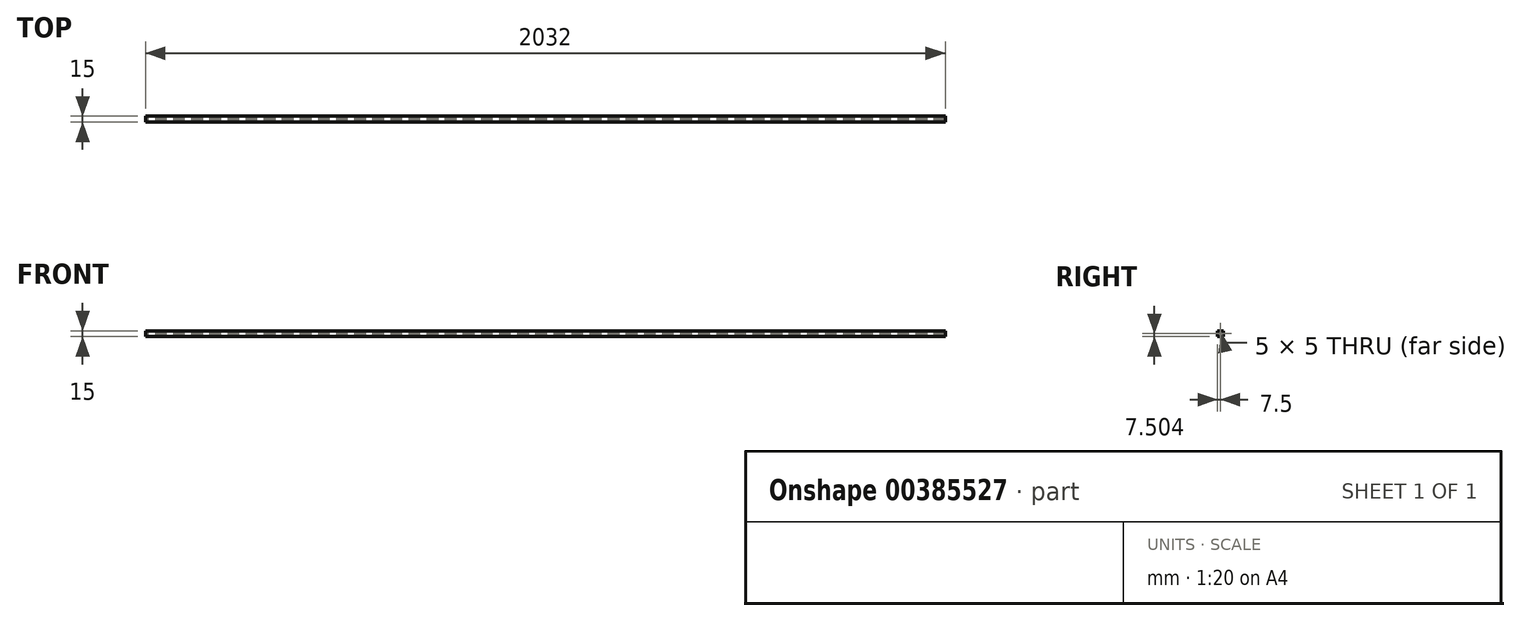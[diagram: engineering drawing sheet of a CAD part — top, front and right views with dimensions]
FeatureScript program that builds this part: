
annotation { "Feature Type Name" : "Feature", "Feature Type Description" : "" }
export const myFeature = defineFeature(function(context is Context, id is Id, definition is map)
    precondition{}
    {
        {
            var Q0;
            Q0=qCreatedBy(makeId("Front.planeOp"),FACE);
            var sketch = newSketch(context, id + "F0", { "sketchPlane" : qUnion([Q0])});
            skLineSegment(sketch, "E0.bottom", {"start": v(-49.25, 39.6) * mm, "end": v(1982.75, 39.6) * mm});
            skLineSegment(sketch, "E0.top", {"start": v(-49.25, 24.6) * mm, "end": v(1982.75, 24.6) * mm});
            skLineSegment(sketch, "E0.left", {"start": v(-49.25, 39.6) * mm, "end": v(-49.25, 24.6) * mm});
            skLineSegment(sketch, "E0.right", {"start": v(1982.75, 39.6) * mm, "end": v(1982.75, 24.6) * mm});
            skSolve(sketch);
        }
        {
            var Q0;
            Q0=makeQuery(id+"F0.imprint","IMPRINT",FACE,{"disambiguationData":[TD([[makeQuery(id+"F0.imprint","IMPRINT",EDGE,{"derivedFrom":sQuery(id+"F0.wireOp",EDGE,"E0.bottom")}),-1.0]])]});
            extrude(context, id + "F1", {"entities" : qUnion([Q0]), "endBound" : BoundingType.SYMMETRIC, "depth" : 15 * mm});
        }
        {
            var Q0;
            Q0=makeQuery(id+"F1.opExtrude","SWEPT_FACE",FACE,{"disambiguationData":[OSD([sQuery(id+"F0.wireOp",EDGE,"E0.left")])]});
            var sketch = newSketch(context, id + "F2", { "sketchPlane" : qUnion([Q0])});
            skLineSegment(sketch, "E1.0", {"start": v(-2.5, 34.6) * mm, "end": v(-2.5, 29.6) * mm});
            skLineSegment(sketch, "E1.1", {"start": v(2.5, 34.6) * mm, "end": v(-2.5, 34.6) * mm});
            skLineSegment(sketch, "E1.2", {"start": v(2.5, 29.6) * mm, "end": v(2.5, 34.6) * mm});
            skLineSegment(sketch, "E1.3", {"start": v(-2.5, 29.6) * mm, "end": v(2.5, 29.6) * mm});
            skSolve(sketch);
        }
        {
            var Q0;
            Q0=makeQuery(id+"F2.imprint","IMPRINT",FACE,{"disambiguationData":[TD([[makeQuery(id+"F2.imprint","IMPRINT",EDGE,{"derivedFrom":sQuery(id+"F2.wireOp",EDGE,"E1.0")}),1.0]])]});
            extrude(context, id + "F3", {"entities" : qUnion([Q0]), "operationType" : NewBodyOperationType.REMOVE, "oppositeDirection" : true, "depth" : 2032 * mm});
        }
    });
